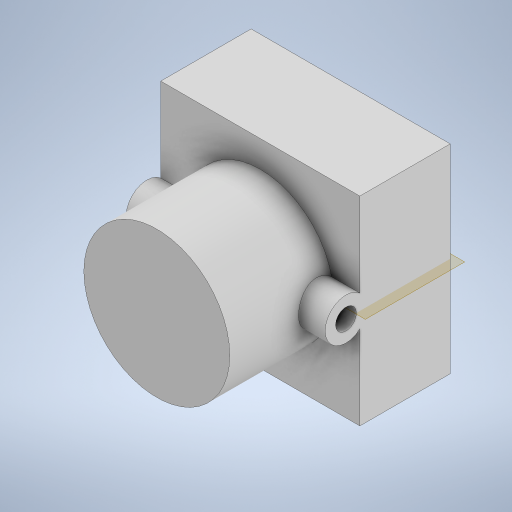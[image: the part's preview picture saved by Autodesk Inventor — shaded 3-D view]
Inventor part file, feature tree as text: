
AUTODESK INVENTOR PART (.ipt)
format: ipt  version: 2023 (Build 270158000, 158)  size: 313,856 bytes
history: native  units: in
note: dims shown in document units (in); Inventor stores cm internally (conversion verified against a paired STEP export)
features: sketch x7, projected_geometry x4, extrude x3, plane x1
ambient origin geometry x8: Origin, YZ Plane, XZ Plane, XY Plane, X Axis, Y Axis, Z Axis, Center Point
bodies: Solid1 (feature_tree)
feature tree (15):
  extrude  "Extrusion1"  Depth=0.752in
  extrude  "Extrusion2"  Depth=0.4331in
  extrude  "Extrusion3"  Depth=0.1575in
  sketch  "Sketch4"  dims[d7=0.3413in d8=0.0in]
  sketch  "Sketch5"  dims[d9=0.5512in]
  sketch  "Sketch6"  dims[d10=0.3909in d11=0.0in]
  plane  "Work Plane1"
  sketch  "Sketch7"  dims[d12=0.7323in d13=0.9139in d14=0.9139in d15=-0.376in]
  sketch  "Sketch1"  dims[d0=0.752in d1=0.752in]
  sketch  "Sketch2"  dims[d2=0.3413in d3=0.0in d4=0.4331in]
  projected_geometry  "Projected Loop1"
  sketch  "Sketch3"  dims[d5=0.0787in d6=0.1575in]
  projected_geometry  "Projected Loop2"
  projected_geometry  "Projected Loop3"
  projected_geometry  "Projected Loop4"
